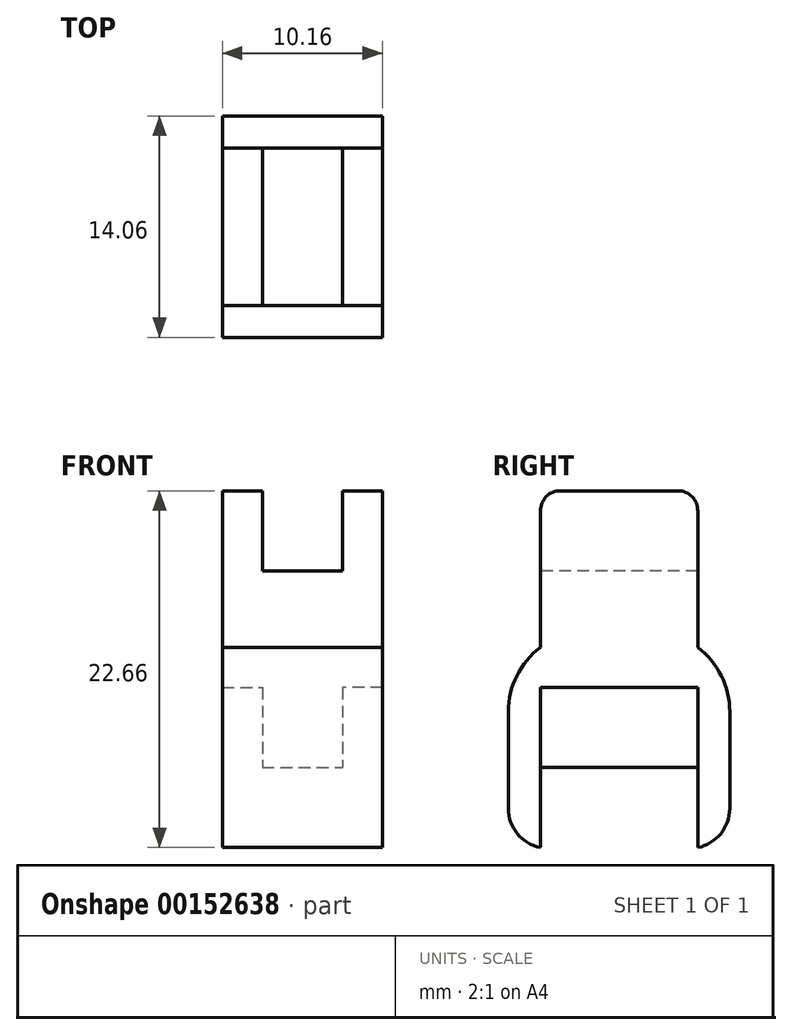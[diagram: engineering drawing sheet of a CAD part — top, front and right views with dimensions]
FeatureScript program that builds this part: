
annotation { "Feature Type Name" : "Feature", "Feature Type Description" : "" }
export const myFeature = defineFeature(function(context is Context, id is Id, definition is map)
    precondition{}
    {
        {
            var Q0;
            Q0=qCreatedBy(makeId("Top.planeOp"),FACE);
            var sketch = newSketch(context, id + "F0", { "sketchPlane" : qUnion([Q0])});
            skLineSegment(sketch, "E0.bottom", {"start": v(0, 0) * mm, "end": v(5.08, 0) * mm});
            skLineSegment(sketch, "E0.top", {"start": v(0, 10) * mm, "end": v(5.08, 10) * mm});
            skLineSegment(sketch, "E0.left", {"start": v(0, 0) * mm, "end": v(0, 10) * mm});
            skLineSegment(sketch, "E0.right", {"start": v(5.08, 0) * mm, "end": v(5.08, 10) * mm});
            skSolve(sketch);
        }
        {
            var Q0;
            Q0 = qSketchRegion(id + "F0", true);
            extrude(context, id + "F1", {"entities" : qUnion([Q0]), "depth" : 12.5 * mm});
        }
        {
            var Q0;
            Q0=makeQuery(id+"F1.opExtrude","SWEPT_FACE",FACE,{"disambiguationData":[OSD([sQuery(id+"F0.wireOp",EDGE,"E0.left")])]});
            var sketch = newSketch(context, id + "F2", { "sketchPlane" : qUnion([Q0])});
            skLineSegment(sketch, "E1.bottom", {"start": v(-10, 12.5) * mm, "end": v(0, 12.5) * mm});
            skLineSegment(sketch, "E1.top", {"start": v(-10, 5.08) * mm, "end": v(0, 5.08) * mm});
            skLineSegment(sketch, "E1.left", {"start": v(-10, 12.5) * mm, "end": v(-10, 5.08) * mm});
            skLineSegment(sketch, "E1.right", {"start": v(0, 12.5) * mm, "end": v(0, 5.08) * mm});
            skSolve(sketch);
        }
        {
            var Q0;
            Q0 = qSketchRegion(id + "F2", true);
            extrude(context, id + "F3", {"entities" : qUnion([Q0]), "operationType" : NewBodyOperationType.ADD, "depth" : 2.54 * mm});
        }
        {
            var Q0;
            Q0=makeQuery(id+"F1.opExtrude","SWEPT_FACE",FACE,{"disambiguationData":[OSD([sQuery(id+"F0.wireOp",EDGE,"E0.right")])]});
            var sketch = newSketch(context, id + "F4", { "sketchPlane" : qUnion([Q0])});
            skLineSegment(sketch, "E2.bottom", {"start": v(0, 12.5) * mm, "end": v(10, 12.5) * mm});
            skLineSegment(sketch, "E2.top", {"start": v(0, 5.08) * mm, "end": v(10, 5.08) * mm});
            skLineSegment(sketch, "E2.left", {"start": v(0, 12.5) * mm, "end": v(0, 5.08) * mm});
            skLineSegment(sketch, "E2.right", {"start": v(10, 12.5) * mm, "end": v(10, 5.08) * mm});
            skSolve(sketch);
        }
        {
            var Q0;
            Q0 = qSketchRegion(id + "F4", true);
            extrude(context, id + "F5", {"entities" : qUnion([Q0]), "operationType" : NewBodyOperationType.ADD, "depth" : 2.54 * mm});
        }
        {
            var Q0;
            Q0=makeQuery(id+"F5.boolean.opBoolean","MERGE",FACE,{"derivedFrom":[makeQuery(id+"F3.boolean.opBoolean","MERGE",FACE,{"derivedFrom":[makeQuery(id+"F1.opExtrude","CAP_FACE",FACE,{"disambiguationData":[OSD([sQuery(id+"F0.wireOp",EDGE,"E0.bottom"),sQuery(id+"F0.wireOp",EDGE,"E0.top"),sQuery(id+"F0.wireOp",EDGE,"E0.left"),sQuery(id+"F0.wireOp",EDGE,"E0.right")])],"isStart":false}),makeQuery(id+"F3.opExtrude","SWEPT_FACE",FACE,{"disambiguationData":[OSD([sQuery(id+"F2.wireOp",EDGE,"E1.bottom")])]})]}),makeQuery(id+"F5.opExtrude","SWEPT_FACE",FACE,{"disambiguationData":[OSD([sQuery(id+"F4.wireOp",EDGE,"E2.bottom")])]})]});
            var sketch = newSketch(context, id + "F6", { "sketchPlane" : qUnion([Q0])});
            skLineSegment(sketch, "E3.bottom", {"start": v(-2.54, 10) * mm, "end": v(0, 10) * mm});
            skLineSegment(sketch, "E3.top", {"start": v(-2.54, 0) * mm, "end": v(0, 0) * mm});
            skLineSegment(sketch, "E3.left", {"start": v(-2.54, 10) * mm, "end": v(-2.54, 0) * mm});
            skLineSegment(sketch, "E3.right", {"start": v(0, 10) * mm, "end": v(0, 0) * mm});
            skLineSegment(sketch, "E4.bottom", {"start": v(7.62, 10) * mm, "end": v(5.08, 10) * mm});
            skLineSegment(sketch, "E4.top", {"start": v(7.62, 0) * mm, "end": v(5.08, 0) * mm});
            skLineSegment(sketch, "E4.left", {"start": v(7.62, 10) * mm, "end": v(7.62, 0) * mm});
            skLineSegment(sketch, "E4.right", {"start": v(5.08, 10) * mm, "end": v(5.08, 0) * mm});
            skSolve(sketch);
        }
        {
            var Q0;
            Q0 = qSketchRegion(id + "F6", true);
            extrude(context, id + "F7", {"entities" : qUnion([Q0]), "operationType" : NewBodyOperationType.ADD, "depth" : 5.08 * mm});
        }
        {
            var Q0;
            Q0=makeQuery(id+"F1.opExtrude","CAP_FACE",FACE,{"disambiguationData":[OSD([sQuery(id+"F0.wireOp",EDGE,"E0.bottom"),sQuery(id+"F0.wireOp",EDGE,"E0.top"),sQuery(id+"F0.wireOp",EDGE,"E0.left"),sQuery(id+"F0.wireOp",EDGE,"E0.right")])],"isStart":true});
            var sketch = newSketch(context, id + "F8", { "sketchPlane" : qUnion([Q0])});
            skLineSegment(sketch, "E5.bottom", {"start": v(-2.54, 2.03) * mm, "end": v(7.62, 2.03) * mm});
            skLineSegment(sketch, "E5.top", {"start": v(-2.54, 0) * mm, "end": v(7.62, 0) * mm});
            skLineSegment(sketch, "E5.left", {"start": v(-2.54, 2.03) * mm, "end": v(-2.54, 0) * mm});
            skLineSegment(sketch, "E5.right", {"start": v(7.62, 2.03) * mm, "end": v(7.62, 0) * mm});
            skLineSegment(sketch, "E6.bottom", {"start": v(-2.54, -10) * mm, "end": v(7.62, -10) * mm});
            skLineSegment(sketch, "E6.top", {"start": v(-2.54, -12.03) * mm, "end": v(7.62, -12.03) * mm});
            skLineSegment(sketch, "E6.left", {"start": v(-2.54, -10) * mm, "end": v(-2.54, -12.03) * mm});
            skLineSegment(sketch, "E6.right", {"start": v(7.62, -10) * mm, "end": v(7.62, -12.03) * mm});
            skSolve(sketch);
        }
        {
            var Q0;
            Q0 = qSketchRegion(id + "F8", true);
            extrude(context, id + "F9", {"entities" : qUnion([Q0]), "operationType" : NewBodyOperationType.ADD, "depth" : 5.08 * mm, "hasSecondDirection" : true, "secondDirectionOppositeDirection" : true, "secondDirectionDepth" : 7.62 * mm});
        }
        {
            var Q0;
            Q0=makeQuery(id+"F9.opExtrude","CAP_EDGE",EDGE,{"disambiguationData":[OSD([sQuery(id+"F8.wireOp",EDGE,"E5.bottom")])],"isStart":true});
            var Q1;
            Q1=makeQuery(id+"F9.opExtrude","CAP_EDGE",EDGE,{"disambiguationData":[OSD([sQuery(id+"F8.wireOp",EDGE,"E6.top")])],"isStart":true});
            fillet(context, id + "F10", {"entities" : qUnion([Q0, Q1]), "radius" : 5.08 * mm, "tangentPropagation" : true, "allowEdgeOverflow" : false});
        }
        {
            var Q0;
            Q0=makeQuery(id+"F7.opExtrude","CAP_EDGE",EDGE,{"disambiguationData":[OSD([sQuery(id+"F6.wireOp",EDGE,"E3.top")])],"isStart":false});
            var Q1;
            Q1=makeQuery(id+"F7.opExtrude","CAP_EDGE",EDGE,{"disambiguationData":[OSD([sQuery(id+"F6.wireOp",EDGE,"E4.top")])],"isStart":false});
            var Q2;
            Q2=makeQuery(id+"F7.opExtrude","CAP_EDGE",EDGE,{"disambiguationData":[OSD([sQuery(id+"F6.wireOp",EDGE,"E4.bottom")])],"isStart":false});
            var Q3;
            Q3=makeQuery(id+"F7.opExtrude","CAP_EDGE",EDGE,{"disambiguationData":[OSD([sQuery(id+"F6.wireOp",EDGE,"E3.bottom")])],"isStart":false});
            fillet(context, id + "F11", {"entities" : qUnion([Q0, Q1, Q2, Q3]), "radius" : 1.27 * mm, "tangentPropagation" : true, "allowEdgeOverflow" : false});
        }
        {
            var Q0;
            Q0=makeQuery(id+"F9.opExtrude","CAP_EDGE",EDGE,{"disambiguationData":[OSD([sQuery(id+"F8.wireOp",EDGE,"E5.bottom")])],"isStart":false});
            var Q1;
            Q1=makeQuery(id+"F9.opExtrude","CAP_EDGE",EDGE,{"disambiguationData":[OSD([sQuery(id+"F8.wireOp",EDGE,"E6.top")])],"isStart":false});
            fillet(context, id + "F12", {"entities" : qUnion([Q0, Q1]), "radius" : 2.54 * mm, "tangentPropagation" : true, "allowEdgeOverflow" : false});
        }
    });
